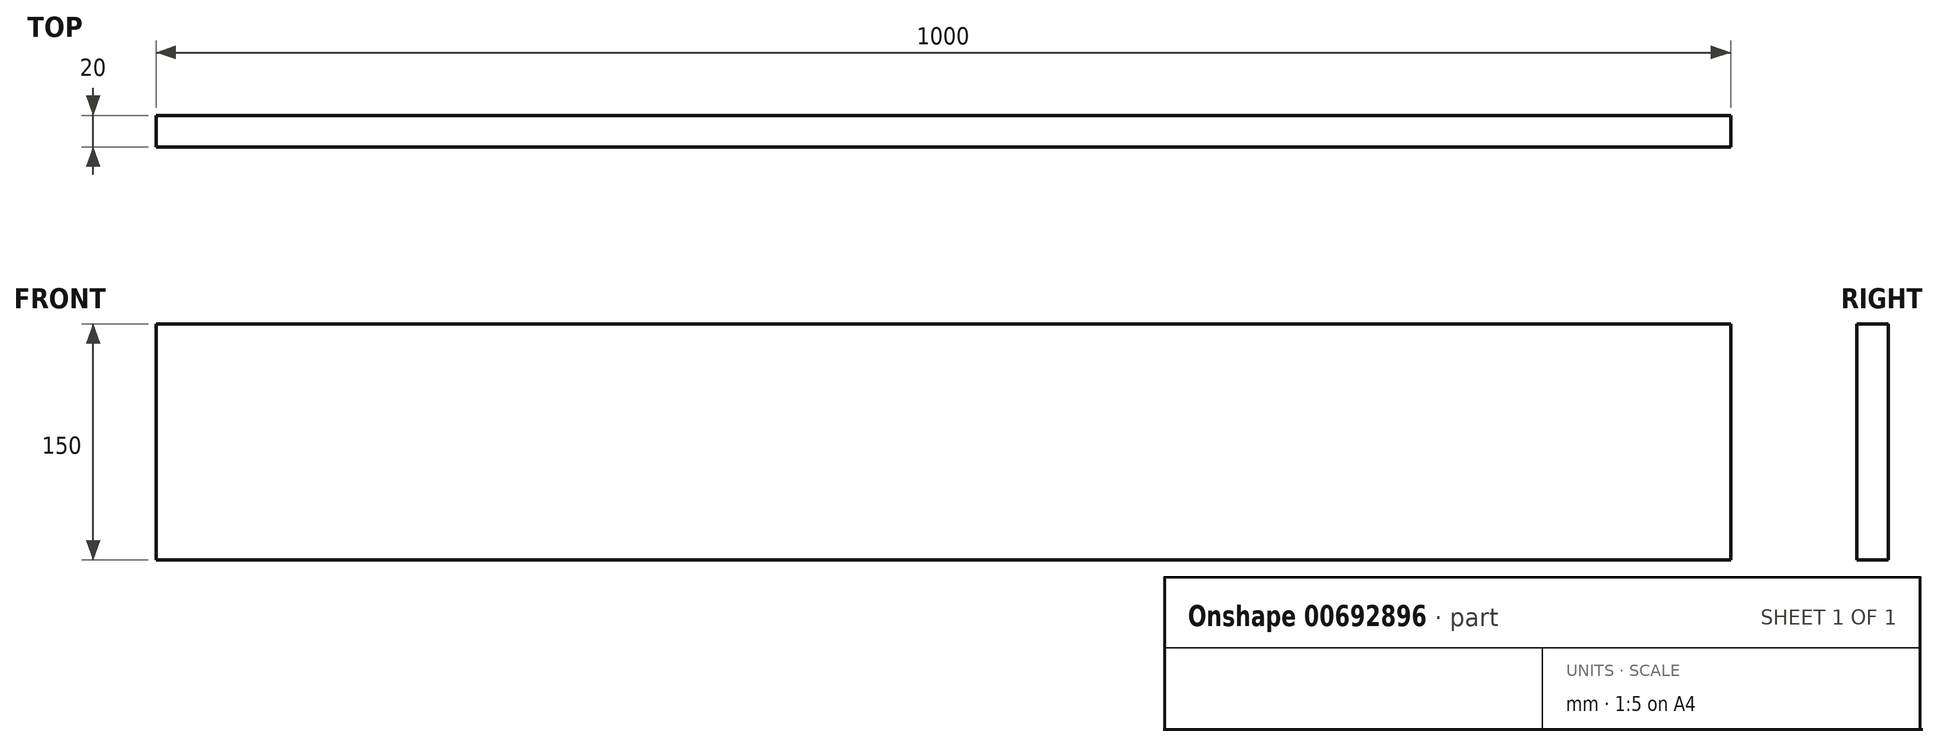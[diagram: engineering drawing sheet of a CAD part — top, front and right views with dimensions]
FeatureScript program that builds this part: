
annotation { "Feature Type Name" : "Feature", "Feature Type Description" : "" }
export const myFeature = defineFeature(function(context is Context, id is Id, definition is map)
    precondition{}
    {
        {
            var Q0;
            Q0=qCreatedBy(makeId("Front.planeOp"),FACE);
            var sketch = newSketch(context, id + "F0", { "sketchPlane" : qUnion([Q0])});
            skLineSegment(sketch, "E0.bottom", {"start": v(0, 150) * mm, "end": v(1000, 150) * mm});
            skLineSegment(sketch, "E0.top", {"start": v(0, 0) * mm, "end": v(1000, 0) * mm});
            skLineSegment(sketch, "E0.left", {"start": v(0, 150) * mm, "end": v(0, 0) * mm});
            skLineSegment(sketch, "E0.right", {"start": v(1000, 150) * mm, "end": v(1000, 0) * mm});
            skSolve(sketch);
        }
        {
            var Q0;
            Q0=makeQuery(id+"F0.imprint","IMPRINT",FACE,{"disambiguationData":[TD([[makeQuery(id+"F0.imprint","IMPRINT",EDGE,{"derivedFrom":sQuery(id+"F0.wireOp",EDGE,"E0.bottom")}),-1.0]])]});
            extrude(context, id + "F1", {"entities" : qUnion([Q0]), "depth" : 20 * mm, "offsetDistance" : 25 * mm});
        }
    });
